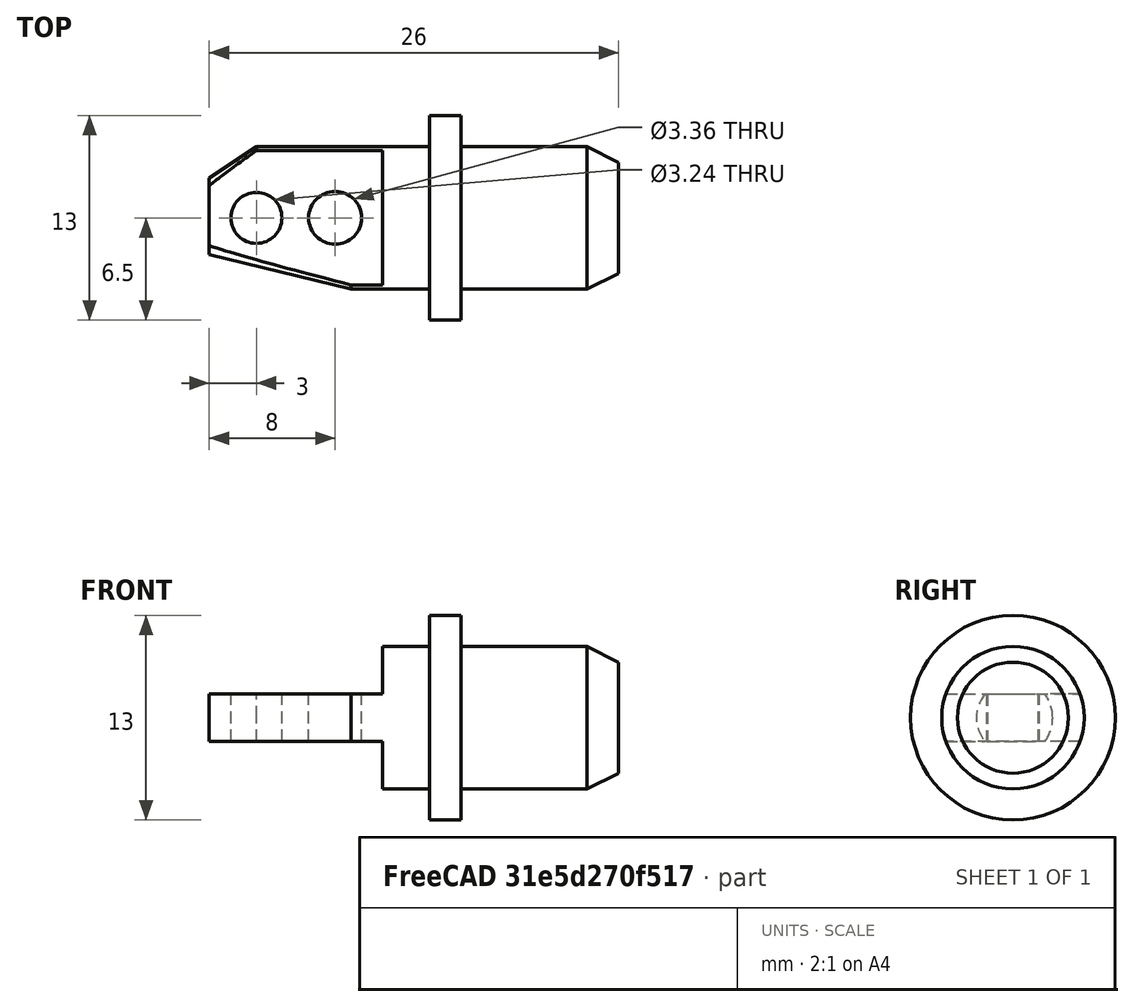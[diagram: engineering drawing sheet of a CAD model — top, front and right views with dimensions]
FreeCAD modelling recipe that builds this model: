
FCSTD DOCUMENT  (FreeCAD 1.0R39285 (Git))
Label: FrontWheelAxleRight
License: All rights reserved
LicenseURL: https://en.wikipedia.org/wiki/All_rights_reserved
objects: PartDesign::SubShapeBinder×1, Part::Mirroring×1, App::Part×1
note: 2 computed .brp shape members not serialized (recipe doc carries the construction recipe); baked Part::Feature solids carry a one-line shape summary decoded from their .brp
EXTERNAL_REF file=FrontWheelAxleLeft.FCStd obj=Part

FEATURE [PartDesign::SubShapeBinder] Binder  label="FrontWheelAxleLeftBody"
  BindCopyOnChange = 0
  BindMode = 0
  ClaimChildren = false
  Context = -> Part [Binder.]
  Fuse = false
  MakeFace = true
  OffsetFill = false
  OffsetIntersection = false
  OffsetJoinType = 0
  OffsetOpenResult = false
  PartialLoad = false
  Refine = true
  Relative = true
  Support = -> [<external FrontWheelAxleLeft.FCStd>#Part[Body.]]
  _Version = 2
FEATURE [Part::Mirroring] Part__Mirroring  label="FrontWheelAxleRightBody"
  Base = (0,0,0)
  Normal = (1,0,0)
  Source = -> Binder
FEATURE [App::Part] Part  label="FrontWheelAxleRightPart"
  Group = -> [Binder,Part__Mirroring]
  Origin = -> Origin
